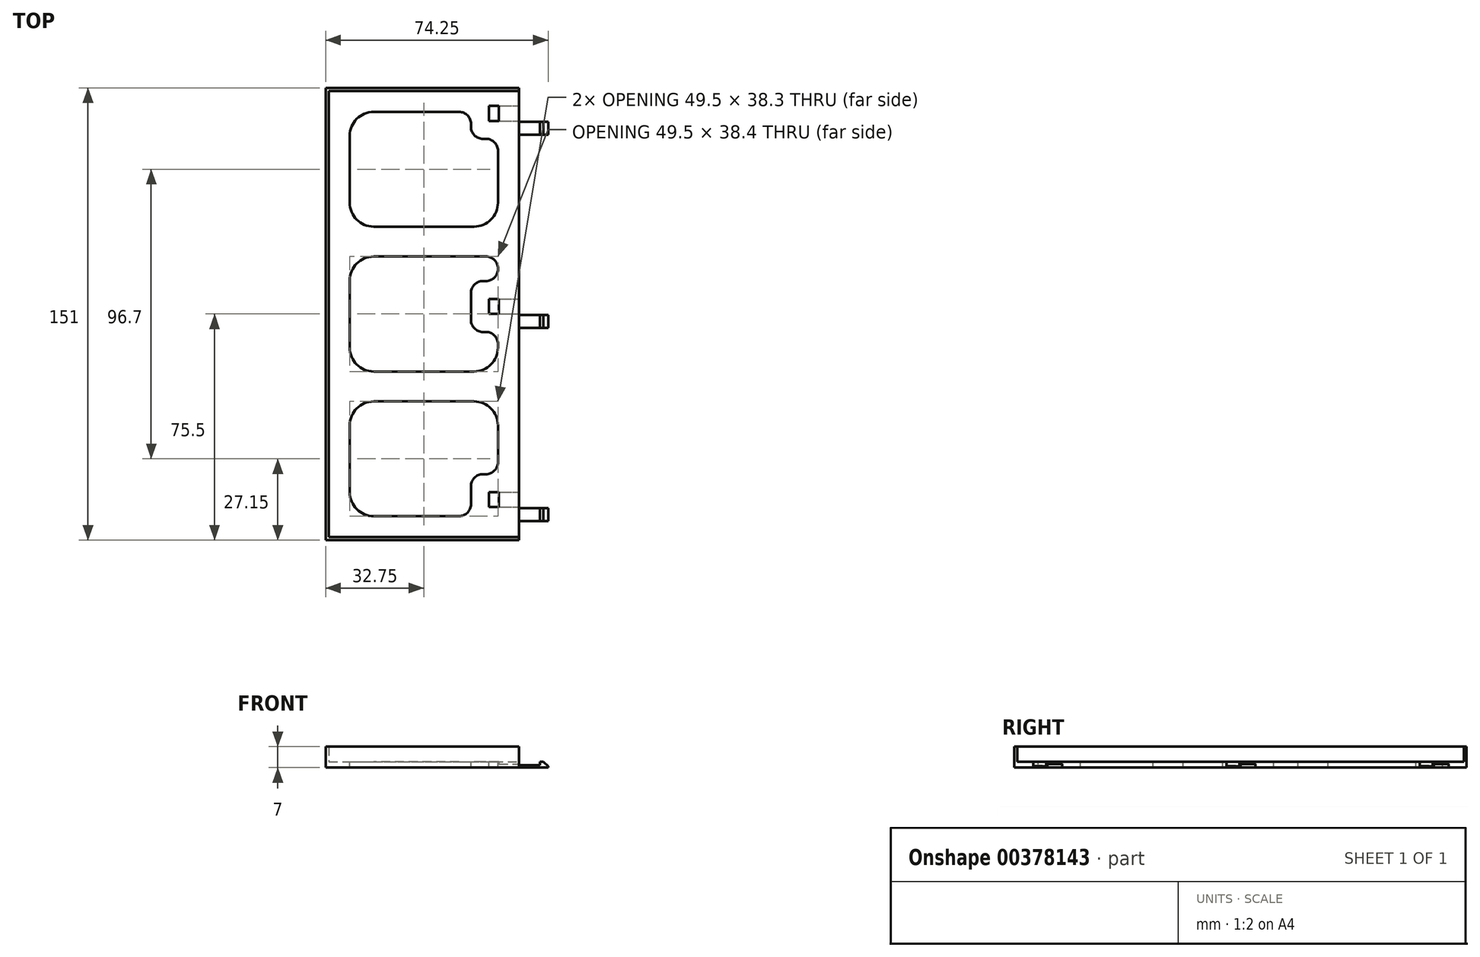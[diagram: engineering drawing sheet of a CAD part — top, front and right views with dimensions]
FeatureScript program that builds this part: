
annotation { "Feature Type Name" : "Feature", "Feature Type Description" : "" }
export const myFeature = defineFeature(function(context is Context, id is Id, definition is map)
    precondition{}
    {
        {
            var Q0;
            Q0=qCreatedBy(makeId("Top.planeOp"),FACE);
            var sketch = newSketch(context, id + "F0", { "sketchPlane" : qUnion([Q0])});
            skLineSegment(sketch, "E0.bottom", {"start": v(0, 0) * mm, "end": v(64.5, 0) * mm});
            skLineSegment(sketch, "E0.top", {"start": v(0, 151) * mm, "end": v(64.5, 151) * mm});
            skLineSegment(sketch, "E0.left", {"start": v(0, 0) * mm, "end": v(0, 151) * mm});
            skLineSegment(sketch, "E0.right", {"start": v(64.5, 0) * mm, "end": v(64.5, 151) * mm});
            skSolve(sketch);
        }
        {
            var Q0;
            Q0=makeQuery(id+"F0.imprint","IMPRINT",FACE,{"disambiguationData":[TD([[makeQuery(id+"F0.imprint","IMPRINT",EDGE,{"derivedFrom":sQuery(id+"F0.wireOp",EDGE,"E0.bottom")}),1.0]])]});
            extrude(context, id + "F1", {"entities" : qUnion([Q0]), "depth" : 2 * mm});
        }
        {
            var Q0;
            Q0=makeQuery(id+"F1.opExtrude","CAP_FACE",FACE,{"disambiguationData":[OSD([sQuery(id+"F0.wireOp",EDGE,"E0.bottom"),sQuery(id+"F0.wireOp",EDGE,"E0.top"),sQuery(id+"F0.wireOp",EDGE,"E0.left"),sQuery(id+"F0.wireOp",EDGE,"E0.right")])],"isStart":false});
            var sketch = newSketch(context, id + "F2", { "sketchPlane" : qUnion([Q0])});
            skLineSegment(sketch, "E1", {"start": v(64.5, 151) * mm, "end": v(0, 151) * mm});
            skLineSegment(sketch, "E2", {"start": v(0, 151) * mm, "end": v(0, 0) * mm});
            skLineSegment(sketch, "E3", {"start": v(0, 0) * mm, "end": v(64.5, 0) * mm});
            skLineSegment(sketch, "E4", {"start": v(64.5, 0) * mm, "end": v(64.5, 1) * mm});
            skLineSegment(sketch, "E5", {"start": v(64.5, 1) * mm, "end": v(1, 1) * mm});
            skLineSegment(sketch, "E6", {"start": v(1, 1) * mm, "end": v(1, 150) * mm});
            skLineSegment(sketch, "E7", {"start": v(1, 150) * mm, "end": v(64.5, 150) * mm});
            skLineSegment(sketch, "E8", {"start": v(64.5, 150) * mm, "end": v(64.5, 151) * mm});
            skSolve(sketch);
        }
        {
            var Q0;
            Q0=makeQuery(id+"F2.imprint","IMPRINT",FACE,{"disambiguationData":[TD([[makeQuery(id+"F2.imprint","IMPRINT",EDGE,{"derivedFrom":sQuery(id+"F2.wireOp",EDGE,"E1")}),-1.0]])]});
            extrude(context, id + "F3", {"entities" : qUnion([Q0]), "operationType" : NewBodyOperationType.ADD, "depth" : 5 * mm});
        }
        {
            var Q0;
            Q0=makeQuery(id+"F3.boolean.opBoolean","MERGE",FACE,{"derivedFrom":[makeQuery(id+"F1.opExtrude","SWEPT_FACE",FACE,{"disambiguationData":[OSD([sQuery(id+"F0.wireOp",EDGE,"E0.right")])]}),makeQuery(id+"F3.opExtrude","SWEPT_FACE",FACE,{"disambiguationData":[OSD([sQuery(id+"F2.wireOp",EDGE,"E4")])]}),makeQuery(id+"F3.opExtrude","SWEPT_FACE",FACE,{"disambiguationData":[OSD([sQuery(id+"F2.wireOp",EDGE,"E8")])]})]});
            var sketch = newSketch(context, id + "F4", { "sketchPlane" : qUnion([Q0])});
            skLineSegment(sketch, "E9.bottom", {"start": v(11, 0) * mm, "end": v(16, 0) * mm});
            skLineSegment(sketch, "E9.top", {"start": v(11, 1.2) * mm, "end": v(16, 1.2) * mm});
            skLineSegment(sketch, "E9.left", {"start": v(11, 0) * mm, "end": v(11, 1.2) * mm});
            skLineSegment(sketch, "E9.right", {"start": v(16, 0) * mm, "end": v(16, 1.2) * mm});
            skLineSegment(sketch, "E10.bottom", {"start": v(140, 0) * mm, "end": v(145, 0) * mm});
            skLineSegment(sketch, "E10.top", {"start": v(140, 1.2) * mm, "end": v(145, 1.2) * mm});
            skLineSegment(sketch, "E10.left", {"start": v(140, 0) * mm, "end": v(140, 1.2) * mm});
            skLineSegment(sketch, "E10.right", {"start": v(145, 0) * mm, "end": v(145, 1.2) * mm});
            skLineSegment(sketch, "E11.bottom", {"start": v(75.5, 0) * mm, "end": v(80.5, 0) * mm});
            skLineSegment(sketch, "E11.top", {"start": v(75.5, 1.2) * mm, "end": v(80.5, 1.2) * mm});
            skLineSegment(sketch, "E11.left", {"start": v(75.5, 0) * mm, "end": v(75.5, 1.2) * mm});
            skLineSegment(sketch, "E11.right", {"start": v(80.5, 0) * mm, "end": v(80.5, 1.2) * mm});
            skSolve(sketch);
        }
        {
            var Q0;
            Q0=makeQuery(id+"F4.imprint","IMPRINT",FACE,{"disambiguationData":[TD([[makeQuery(id+"F4.imprint","IMPRINT",EDGE,{"derivedFrom":sQuery(id+"F4.wireOp",EDGE,"E10.bottom")}),1.0]])]});
            var Q1;
            Q1=makeQuery(id+"F4.imprint","IMPRINT",FACE,{"disambiguationData":[TD([[makeQuery(id+"F4.imprint","IMPRINT",EDGE,{"derivedFrom":sQuery(id+"F4.wireOp",EDGE,"E11.bottom")}),1.0]])]});
            var Q2;
            Q2=makeQuery(id+"F4.imprint","IMPRINT",FACE,{"disambiguationData":[TD([[makeQuery(id+"F4.imprint","IMPRINT",EDGE,{"derivedFrom":sQuery(id+"F4.wireOp",EDGE,"E9.bottom")}),1.0]])]});
            extrude(context, id + "F5", {"entities" : qUnion([Q0, Q1, Q2]), "operationType" : NewBodyOperationType.REMOVE, "oppositeDirection" : true, "depth" : 10 * mm});
        }
        {
            var Q0;
            Q0=makeQuery(id+"F3.boolean.opBoolean","MERGE",FACE,{"derivedFrom":[makeQuery(id+"F1.opExtrude","SWEPT_FACE",FACE,{"disambiguationData":[OSD([sQuery(id+"F0.wireOp",EDGE,"E0.right")])]}),makeQuery(id+"F3.opExtrude","SWEPT_FACE",FACE,{"disambiguationData":[OSD([sQuery(id+"F2.wireOp",EDGE,"E4")])]}),makeQuery(id+"F3.opExtrude","SWEPT_FACE",FACE,{"disambiguationData":[OSD([sQuery(id+"F2.wireOp",EDGE,"E8")])]})]});
            var sketch = newSketch(context, id + "F6", { "sketchPlane" : qUnion([Q0])});
            skLineSegment(sketch, "E12.bottom", {"start": v(6.35, 0) * mm, "end": v(10.65, 0) * mm});
            skLineSegment(sketch, "E12.top", {"start": v(6.35, 0.8) * mm, "end": v(10.65, 0.8) * mm});
            skLineSegment(sketch, "E12.left", {"start": v(6.35, 0) * mm, "end": v(6.35, 0.8) * mm});
            skLineSegment(sketch, "E12.right", {"start": v(10.65, 0) * mm, "end": v(10.65, 0.8) * mm});
            skLineSegment(sketch, "E13.bottom", {"start": v(70.85, 0) * mm, "end": v(75.15, 0) * mm});
            skLineSegment(sketch, "E13.top", {"start": v(70.85, 0.8) * mm, "end": v(75.15, 0.8) * mm});
            skLineSegment(sketch, "E13.left", {"start": v(70.85, 0) * mm, "end": v(70.85, 0.8) * mm});
            skLineSegment(sketch, "E13.right", {"start": v(75.15, 0) * mm, "end": v(75.15, 0.8) * mm});
            skLineSegment(sketch, "E14.bottom", {"start": v(135.35, 0) * mm, "end": v(139.65, 0) * mm});
            skLineSegment(sketch, "E14.top", {"start": v(135.35, 0.8) * mm, "end": v(139.65, 0.8) * mm});
            skLineSegment(sketch, "E14.left", {"start": v(135.35, 0) * mm, "end": v(135.35, 0.8) * mm});
            skLineSegment(sketch, "E14.right", {"start": v(139.65, 0) * mm, "end": v(139.65, 0.8) * mm});
            skSolve(sketch);
        }
        {
            var Q0;
            Q0=makeQuery(id+"F6.imprint","IMPRINT",FACE,{"disambiguationData":[TD([[makeQuery(id+"F6.imprint","IMPRINT",EDGE,{"derivedFrom":sQuery(id+"F6.wireOp",EDGE,"E12.bottom")}),1.0]])]});
            var Q1;
            Q1=makeQuery(id+"F6.imprint","IMPRINT",FACE,{"disambiguationData":[TD([[makeQuery(id+"F6.imprint","IMPRINT",EDGE,{"derivedFrom":sQuery(id+"F6.wireOp",EDGE,"E13.bottom")}),1.0]])]});
            var Q2;
            Q2=makeQuery(id+"F6.imprint","IMPRINT",FACE,{"disambiguationData":[TD([[makeQuery(id+"F6.imprint","IMPRINT",EDGE,{"derivedFrom":sQuery(id+"F6.wireOp",EDGE,"E14.bottom")}),1.0]])]});
            extrude(context, id + "F7", {"entities" : qUnion([Q0, Q1, Q2]), "operationType" : NewBodyOperationType.ADD, "depth" : 9.75 * mm});
        }
        {
            var Q0;
            Q0=makeQuery(id+"F7.opExtrude","SWEPT_FACE",FACE,{"disambiguationData":[OSD([sQuery(id+"F6.wireOp",EDGE,"E12.top")])]});
            var sketch = newSketch(context, id + "F8", { "sketchPlane" : qUnion([Q0])});
            skLineSegment(sketch, "E15.bottom", {"start": v(74.25, 6.35) * mm, "end": v(71.5, 6.35) * mm});
            skLineSegment(sketch, "E15.top", {"start": v(74.25, 10.65) * mm, "end": v(71.5, 10.65) * mm});
            skLineSegment(sketch, "E15.left", {"start": v(74.25, 6.35) * mm, "end": v(74.25, 10.65) * mm});
            skLineSegment(sketch, "E15.right", {"start": v(71.5, 6.35) * mm, "end": v(71.5, 10.65) * mm});
            skSolve(sketch);
        }
        {
            var Q0;
            Q0=makeQuery(id+"F8.imprint","IMPRINT",FACE,{"disambiguationData":[TD([[makeQuery(id+"F8.imprint","IMPRINT",EDGE,{"derivedFrom":sQuery(id+"F8.wireOp",EDGE,"E15.bottom")}),-1.0]])]});
            extrude(context, id + "F9", {"entities" : qUnion([Q0]), "operationType" : NewBodyOperationType.ADD, "depth" : 1.2 * mm});
        }
        {
            var Q0;
            Q0=makeQuery(id+"F7.opExtrude","SWEPT_FACE",FACE,{"disambiguationData":[OSD([sQuery(id+"F6.wireOp",EDGE,"E13.top")])]});
            var sketch = newSketch(context, id + "F10", { "sketchPlane" : qUnion([Q0])});
            skLineSegment(sketch, "E16.bottom", {"start": v(74.25, 70.85) * mm, "end": v(71.5, 70.85) * mm});
            skLineSegment(sketch, "E16.top", {"start": v(74.25, 75.15) * mm, "end": v(71.5, 75.15) * mm});
            skLineSegment(sketch, "E16.left", {"start": v(74.25, 70.85) * mm, "end": v(74.25, 75.15) * mm});
            skLineSegment(sketch, "E16.right", {"start": v(71.5, 70.85) * mm, "end": v(71.5, 75.15) * mm});
            skSolve(sketch);
        }
        {
            var Q0;
            Q0=makeQuery(id+"F10.imprint","IMPRINT",FACE,{"disambiguationData":[TD([[makeQuery(id+"F10.imprint","IMPRINT",EDGE,{"derivedFrom":sQuery(id+"F10.wireOp",EDGE,"E16.bottom")}),-1.0]])]});
            extrude(context, id + "F11", {"entities" : qUnion([Q0]), "operationType" : NewBodyOperationType.ADD, "depth" : 1.2 * mm});
        }
        {
            var Q0;
            Q0=makeQuery(id+"F7.opExtrude","SWEPT_FACE",FACE,{"disambiguationData":[OSD([sQuery(id+"F6.wireOp",EDGE,"E14.top")])]});
            var sketch = newSketch(context, id + "F12", { "sketchPlane" : qUnion([Q0])});
            skLineSegment(sketch, "E17.bottom", {"start": v(74.25, 135.35) * mm, "end": v(71.5, 135.35) * mm});
            skLineSegment(sketch, "E17.top", {"start": v(74.25, 139.65) * mm, "end": v(71.5, 139.65) * mm});
            skLineSegment(sketch, "E17.left", {"start": v(74.25, 135.35) * mm, "end": v(74.25, 139.65) * mm});
            skLineSegment(sketch, "E17.right", {"start": v(71.5, 135.35) * mm, "end": v(71.5, 139.65) * mm});
            skSolve(sketch);
        }
        {
            var Q0;
            Q0=makeQuery(id+"F12.imprint","IMPRINT",FACE,{"disambiguationData":[TD([[makeQuery(id+"F12.imprint","IMPRINT",EDGE,{"derivedFrom":sQuery(id+"F12.wireOp",EDGE,"E17.bottom")}),-1.0]])]});
            extrude(context, id + "F13", {"entities" : qUnion([Q0]), "operationType" : NewBodyOperationType.ADD, "depth" : 1.2 * mm});
        }
        {
            var Q0;
            Q0=makeQuery(id+"F5.boolean.opBoolean","COPY",FACE,{"derivedFrom":makeQuery(id+"F5.opExtrude","SWEPT_FACE",FACE,{"disambiguationData":[OSD([sQuery(id+"F4.wireOp",EDGE,"E9.top")])]})});
            var sketch = newSketch(context, id + "F14", { "sketchPlane" : qUnion([Q0])});
            skLineSegment(sketch, "E18.bottom", {"start": v(54.5, -11) * mm, "end": v(57.8, -11) * mm});
            skLineSegment(sketch, "E18.top", {"start": v(54.5, -16) * mm, "end": v(57.8, -16) * mm});
            skLineSegment(sketch, "E18.left", {"start": v(54.5, -11) * mm, "end": v(54.5, -16) * mm});
            skLineSegment(sketch, "E18.right", {"start": v(57.8, -11) * mm, "end": v(57.8, -16) * mm});
            skSolve(sketch);
        }
        {
            var Q0;
            Q0=makeQuery(id+"F14.imprint","IMPRINT",FACE,{"disambiguationData":[TD([[makeQuery(id+"F14.imprint","IMPRINT",EDGE,{"derivedFrom":sQuery(id+"F14.wireOp",EDGE,"E18.bottom")}),-1.0]])]});
            extrude(context, id + "F15", {"entities" : qUnion([Q0]), "operationType" : NewBodyOperationType.REMOVE, "endBound" : BoundingType.THROUGH_ALL, "oppositeDirection" : true, "depth" : 25 * mm});
        }
        {
            var Q0;
            Q0=makeQuery(id+"F5.boolean.opBoolean","COPY",FACE,{"derivedFrom":makeQuery(id+"F5.opExtrude","SWEPT_FACE",FACE,{"disambiguationData":[OSD([sQuery(id+"F4.wireOp",EDGE,"E11.top")])]})});
            var sketch = newSketch(context, id + "F16", { "sketchPlane" : qUnion([Q0])});
            skLineSegment(sketch, "E19.bottom", {"start": v(54.5, -75.5) * mm, "end": v(57.8, -75.5) * mm});
            skLineSegment(sketch, "E19.top", {"start": v(54.5, -80.5) * mm, "end": v(57.8, -80.5) * mm});
            skLineSegment(sketch, "E19.left", {"start": v(54.5, -75.5) * mm, "end": v(54.5, -80.5) * mm});
            skLineSegment(sketch, "E19.right", {"start": v(57.8, -75.5) * mm, "end": v(57.8, -80.5) * mm});
            skSolve(sketch);
        }
        {
            var Q0;
            Q0=makeQuery(id+"F16.imprint","IMPRINT",FACE,{"disambiguationData":[TD([[makeQuery(id+"F16.imprint","IMPRINT",EDGE,{"derivedFrom":sQuery(id+"F16.wireOp",EDGE,"E19.bottom")}),-1.0]])]});
            extrude(context, id + "F17", {"entities" : qUnion([Q0]), "operationType" : NewBodyOperationType.REMOVE, "endBound" : BoundingType.THROUGH_ALL, "oppositeDirection" : true, "depth" : 25 * mm});
        }
        {
            var Q0;
            Q0=makeQuery(id+"F5.boolean.opBoolean","COPY",FACE,{"derivedFrom":makeQuery(id+"F5.opExtrude","SWEPT_FACE",FACE,{"disambiguationData":[OSD([sQuery(id+"F4.wireOp",EDGE,"E10.top")])]})});
            var sketch = newSketch(context, id + "F18", { "sketchPlane" : qUnion([Q0])});
            skLineSegment(sketch, "E20.bottom", {"start": v(54.5, -140) * mm, "end": v(57.8, -140) * mm});
            skLineSegment(sketch, "E20.top", {"start": v(54.5, -145) * mm, "end": v(57.8, -145) * mm});
            skLineSegment(sketch, "E20.left", {"start": v(54.5, -140) * mm, "end": v(54.5, -145) * mm});
            skLineSegment(sketch, "E20.right", {"start": v(57.8, -140) * mm, "end": v(57.8, -145) * mm});
            skSolve(sketch);
        }
        {
            var Q0;
            Q0=makeQuery(id+"F18.imprint","IMPRINT",FACE,{"disambiguationData":[TD([[makeQuery(id+"F18.imprint","IMPRINT",EDGE,{"derivedFrom":sQuery(id+"F18.wireOp",EDGE,"E20.bottom")}),-1.0]])]});
            extrude(context, id + "F19", {"entities" : qUnion([Q0]), "operationType" : NewBodyOperationType.REMOVE, "endBound" : BoundingType.THROUGH_ALL, "oppositeDirection" : true, "depth" : 25 * mm});
        }
        {
            var Q0;
            Q0=makeQuery(id+"F9.opExtrude","CAP_EDGE",EDGE,{"disambiguationData":[OSD([sQuery(id+"F8.wireOp",EDGE,"E15.left")])],"isStart":false});
            var Q1;
            Q1=makeQuery(id+"F11.opExtrude","CAP_EDGE",EDGE,{"disambiguationData":[OSD([sQuery(id+"F10.wireOp",EDGE,"E16.left")])],"isStart":false});
            var Q2;
            Q2=makeQuery(id+"F13.opExtrude","CAP_EDGE",EDGE,{"disambiguationData":[OSD([sQuery(id+"F12.wireOp",EDGE,"E17.left")])],"isStart":false});
            chamfer(context, id + "F20", {"entities" : qUnion([Q0, Q1, Q2]), "width" : 1.6 * mm, "tangentPropagation" : true});
        }
        {
            var Q0;
            Q0=makeQuery(id+"F1.opExtrude","CAP_FACE",FACE,{"disambiguationData":[OSD([sQuery(id+"F0.wireOp",EDGE,"E0.bottom"),sQuery(id+"F0.wireOp",EDGE,"E0.top"),sQuery(id+"F0.wireOp",EDGE,"E0.left"),sQuery(id+"F0.wireOp",EDGE,"E0.right")])],"isStart":false});
            var sketch = newSketch(context, id + "F21", { "sketchPlane" : qUnion([Q0])});
            skLineSegment(sketch, "E21", {"start": v(8, 8) * mm, "end": v(8, 46.3) * mm});
            skLineSegment(sketch, "E22", {"start": v(8, 46.3) * mm, "end": v(57.5, 46.3) * mm});
            skLineSegment(sketch, "E23", {"start": v(57.5, 46.3) * mm, "end": v(57.5, 22) * mm});
            skLineSegment(sketch, "E24", {"start": v(57.5, 22) * mm, "end": v(48.5, 22) * mm});
            skLineSegment(sketch, "E25", {"start": v(48.5, 22) * mm, "end": v(48.5, 8) * mm});
            skLineSegment(sketch, "E26", {"start": v(48.5, 8) * mm, "end": v(8, 8) * mm});
            skLineSegment(sketch, "E27", {"start": v(57.5, 56.3) * mm, "end": v(8, 56.3) * mm});
            skLineSegment(sketch, "E28", {"start": v(8, 56.3) * mm, "end": v(8, 94.7) * mm});
            skLineSegment(sketch, "E29", {"start": v(8, 94.7) * mm, "end": v(57.5, 94.7) * mm});
            skLineSegment(sketch, "E30", {"start": v(57.5, 94.7) * mm, "end": v(57.5, 86.5) * mm});
            skLineSegment(sketch, "E31", {"start": v(57.5, 86.5) * mm, "end": v(48.5, 86.5) * mm});
            skLineSegment(sketch, "E32", {"start": v(48.5, 86.5) * mm, "end": v(48.5, 69.5) * mm});
            skLineSegment(sketch, "E33", {"start": v(48.5, 69.5) * mm, "end": v(57.5, 69.5) * mm});
            skLineSegment(sketch, "E34", {"start": v(57.5, 69.5) * mm, "end": v(57.5, 56.3) * mm});
            skLineSegment(sketch, "E35", {"start": v(8, 104.7) * mm, "end": v(8, 143) * mm});
            skLineSegment(sketch, "E36", {"start": v(8, 143) * mm, "end": v(48.5, 143) * mm});
            skLineSegment(sketch, "E37", {"start": v(48.5, 143) * mm, "end": v(48.5, 134) * mm});
            skLineSegment(sketch, "E38", {"start": v(48.5, 134) * mm, "end": v(57.5, 134) * mm});
            skLineSegment(sketch, "E39", {"start": v(57.5, 134) * mm, "end": v(57.5, 104.7) * mm});
            skLineSegment(sketch, "E40", {"start": v(57.5, 104.7) * mm, "end": v(8, 104.7) * mm});
            skSolve(sketch);
        }
        {
            var Q0;
            Q0=makeQuery(id+"F21.imprint","IMPRINT",FACE,{"disambiguationData":[TD([[makeQuery(id+"F21.imprint","IMPRINT",EDGE,{"derivedFrom":sQuery(id+"F21.wireOp",EDGE,"E35")}),-1.0]])]});
            var Q1;
            Q1=makeQuery(id+"F21.imprint","IMPRINT",FACE,{"disambiguationData":[TD([[makeQuery(id+"F21.imprint","IMPRINT",EDGE,{"derivedFrom":sQuery(id+"F21.wireOp",EDGE,"E27")}),-1.0]])]});
            var Q2;
            Q2=makeQuery(id+"F21.imprint","IMPRINT",FACE,{"disambiguationData":[TD([[makeQuery(id+"F21.imprint","IMPRINT",EDGE,{"derivedFrom":sQuery(id+"F21.wireOp",EDGE,"E21")}),-1.0]])]});
            extrude(context, id + "F22", {"entities" : qUnion([Q0, Q1, Q2]), "operationType" : NewBodyOperationType.REMOVE, "endBound" : BoundingType.THROUGH_ALL, "oppositeDirection" : true, "depth" : 25 * mm});
        }
        {
            var Q0;
            Q0=makeQuery(id+"F22.boolean.opBoolean","COPY",EDGE,{"derivedFrom":makeQuery(id+"F22.opExtrude","SWEPT_EDGE",EDGE,{"disambiguationData":[OSD([sQuery(id+"F21.wireOp",EDGE,"E37"),sQuery(id+"F21.wireOp",EDGE,"E38")])]})});
            var Q1;
            Q1=makeQuery(id+"F22.boolean.opBoolean","COPY",EDGE,{"derivedFrom":makeQuery(id+"F22.opExtrude","SWEPT_EDGE",EDGE,{"disambiguationData":[OSD([sQuery(id+"F21.wireOp",EDGE,"E36"),sQuery(id+"F21.wireOp",EDGE,"E37")])]})});
            var Q2;
            Q2=makeQuery(id+"F22.boolean.opBoolean","COPY",EDGE,{"derivedFrom":makeQuery(id+"F22.opExtrude","SWEPT_EDGE",EDGE,{"disambiguationData":[OSD([sQuery(id+"F21.wireOp",EDGE,"E38"),sQuery(id+"F21.wireOp",EDGE,"E39")])]})});
            var Q3;
            Q3=makeQuery(id+"F22.boolean.opBoolean","COPY",EDGE,{"derivedFrom":makeQuery(id+"F22.opExtrude","SWEPT_EDGE",EDGE,{"disambiguationData":[OSD([sQuery(id+"F21.wireOp",EDGE,"E29"),sQuery(id+"F21.wireOp",EDGE,"E30")])]})});
            var Q4;
            Q4=makeQuery(id+"F22.boolean.opBoolean","COPY",EDGE,{"derivedFrom":makeQuery(id+"F22.opExtrude","SWEPT_EDGE",EDGE,{"disambiguationData":[OSD([sQuery(id+"F21.wireOp",EDGE,"E31"),sQuery(id+"F21.wireOp",EDGE,"E32")])]})});
            var Q5;
            Q5=makeQuery(id+"F22.boolean.opBoolean","COPY",EDGE,{"derivedFrom":makeQuery(id+"F22.opExtrude","SWEPT_EDGE",EDGE,{"disambiguationData":[OSD([sQuery(id+"F21.wireOp",EDGE,"E32"),sQuery(id+"F21.wireOp",EDGE,"E33")])]})});
            var Q6;
            Q6=makeQuery(id+"F22.boolean.opBoolean","COPY",EDGE,{"derivedFrom":makeQuery(id+"F22.opExtrude","SWEPT_EDGE",EDGE,{"disambiguationData":[OSD([sQuery(id+"F21.wireOp",EDGE,"E33"),sQuery(id+"F21.wireOp",EDGE,"E34")])]})});
            var Q7;
            Q7=makeQuery(id+"F22.boolean.opBoolean","COPY",EDGE,{"derivedFrom":makeQuery(id+"F22.opExtrude","SWEPT_EDGE",EDGE,{"disambiguationData":[OSD([sQuery(id+"F21.wireOp",EDGE,"E24"),sQuery(id+"F21.wireOp",EDGE,"E25")])]})});
            var Q8;
            Q8=makeQuery(id+"F22.boolean.opBoolean","COPY",EDGE,{"derivedFrom":makeQuery(id+"F22.opExtrude","SWEPT_EDGE",EDGE,{"disambiguationData":[OSD([sQuery(id+"F21.wireOp",EDGE,"E30"),sQuery(id+"F21.wireOp",EDGE,"E31")])]})});
            var Q9;
            Q9=makeQuery(id+"F22.boolean.opBoolean","COPY",EDGE,{"derivedFrom":makeQuery(id+"F22.opExtrude","SWEPT_EDGE",EDGE,{"disambiguationData":[OSD([sQuery(id+"F21.wireOp",EDGE,"E23"),sQuery(id+"F21.wireOp",EDGE,"E24")])]})});
            var Q10;
            Q10=makeQuery(id+"F22.boolean.opBoolean","COPY",EDGE,{"derivedFrom":makeQuery(id+"F22.opExtrude","SWEPT_EDGE",EDGE,{"disambiguationData":[OSD([sQuery(id+"F21.wireOp",EDGE,"E25"),sQuery(id+"F21.wireOp",EDGE,"E26")])]})});
            fillet(context, id + "F23", {"entities" : qUnion([Q0, Q1, Q2, Q3, Q4, Q5, Q6, Q7, Q8, Q9, Q10]), "radius" : 4 * mm, "tangentPropagation" : true, "allowEdgeOverflow" : false});
        }
        {
            var Q0;
            Q0=makeQuery(id+"F22.boolean.opBoolean","COPY",EDGE,{"derivedFrom":makeQuery(id+"F22.opExtrude","SWEPT_EDGE",EDGE,{"disambiguationData":[OSD([sQuery(id+"F21.wireOp",EDGE,"E21"),sQuery(id+"F21.wireOp",EDGE,"E26")])]})});
            var Q1;
            Q1=makeQuery(id+"F22.boolean.opBoolean","COPY",EDGE,{"derivedFrom":makeQuery(id+"F22.opExtrude","SWEPT_EDGE",EDGE,{"disambiguationData":[OSD([sQuery(id+"F21.wireOp",EDGE,"E27"),sQuery(id+"F21.wireOp",EDGE,"E28")])]})});
            var Q2;
            Q2=makeQuery(id+"F22.boolean.opBoolean","COPY",EDGE,{"derivedFrom":makeQuery(id+"F22.opExtrude","SWEPT_EDGE",EDGE,{"disambiguationData":[OSD([sQuery(id+"F21.wireOp",EDGE,"E35"),sQuery(id+"F21.wireOp",EDGE,"E40")])]})});
            var Q3;
            Q3=makeQuery(id+"F22.boolean.opBoolean","COPY",EDGE,{"derivedFrom":makeQuery(id+"F22.opExtrude","SWEPT_EDGE",EDGE,{"disambiguationData":[OSD([sQuery(id+"F21.wireOp",EDGE,"E21"),sQuery(id+"F21.wireOp",EDGE,"E22")])]})});
            var Q4;
            Q4=makeQuery(id+"F22.boolean.opBoolean","COPY",EDGE,{"derivedFrom":makeQuery(id+"F22.opExtrude","SWEPT_EDGE",EDGE,{"disambiguationData":[OSD([sQuery(id+"F21.wireOp",EDGE,"E28"),sQuery(id+"F21.wireOp",EDGE,"E29")])]})});
            var Q5;
            Q5=makeQuery(id+"F22.boolean.opBoolean","COPY",EDGE,{"derivedFrom":makeQuery(id+"F22.opExtrude","SWEPT_EDGE",EDGE,{"disambiguationData":[OSD([sQuery(id+"F21.wireOp",EDGE,"E35"),sQuery(id+"F21.wireOp",EDGE,"E36")])]})});
            var Q6;
            Q6=makeQuery(id+"F22.boolean.opBoolean","COPY",EDGE,{"derivedFrom":makeQuery(id+"F22.opExtrude","SWEPT_EDGE",EDGE,{"disambiguationData":[OSD([sQuery(id+"F21.wireOp",EDGE,"E39"),sQuery(id+"F21.wireOp",EDGE,"E40")])]})});
            var Q7;
            Q7=makeQuery(id+"F22.boolean.opBoolean","COPY",EDGE,{"derivedFrom":makeQuery(id+"F22.opExtrude","SWEPT_EDGE",EDGE,{"disambiguationData":[OSD([sQuery(id+"F21.wireOp",EDGE,"E27"),sQuery(id+"F21.wireOp",EDGE,"E34")])]})});
            var Q8;
            Q8=makeQuery(id+"F22.boolean.opBoolean","COPY",EDGE,{"derivedFrom":makeQuery(id+"F22.opExtrude","SWEPT_EDGE",EDGE,{"disambiguationData":[OSD([sQuery(id+"F21.wireOp",EDGE,"E22"),sQuery(id+"F21.wireOp",EDGE,"E23")])]})});
            fillet(context, id + "F24", {"entities" : qUnion([Q0, Q1, Q2, Q3, Q4, Q5, Q6, Q7, Q8]), "radius" : 8 * mm, "tangentPropagation" : true, "allowEdgeOverflow" : false});
        }
    });
